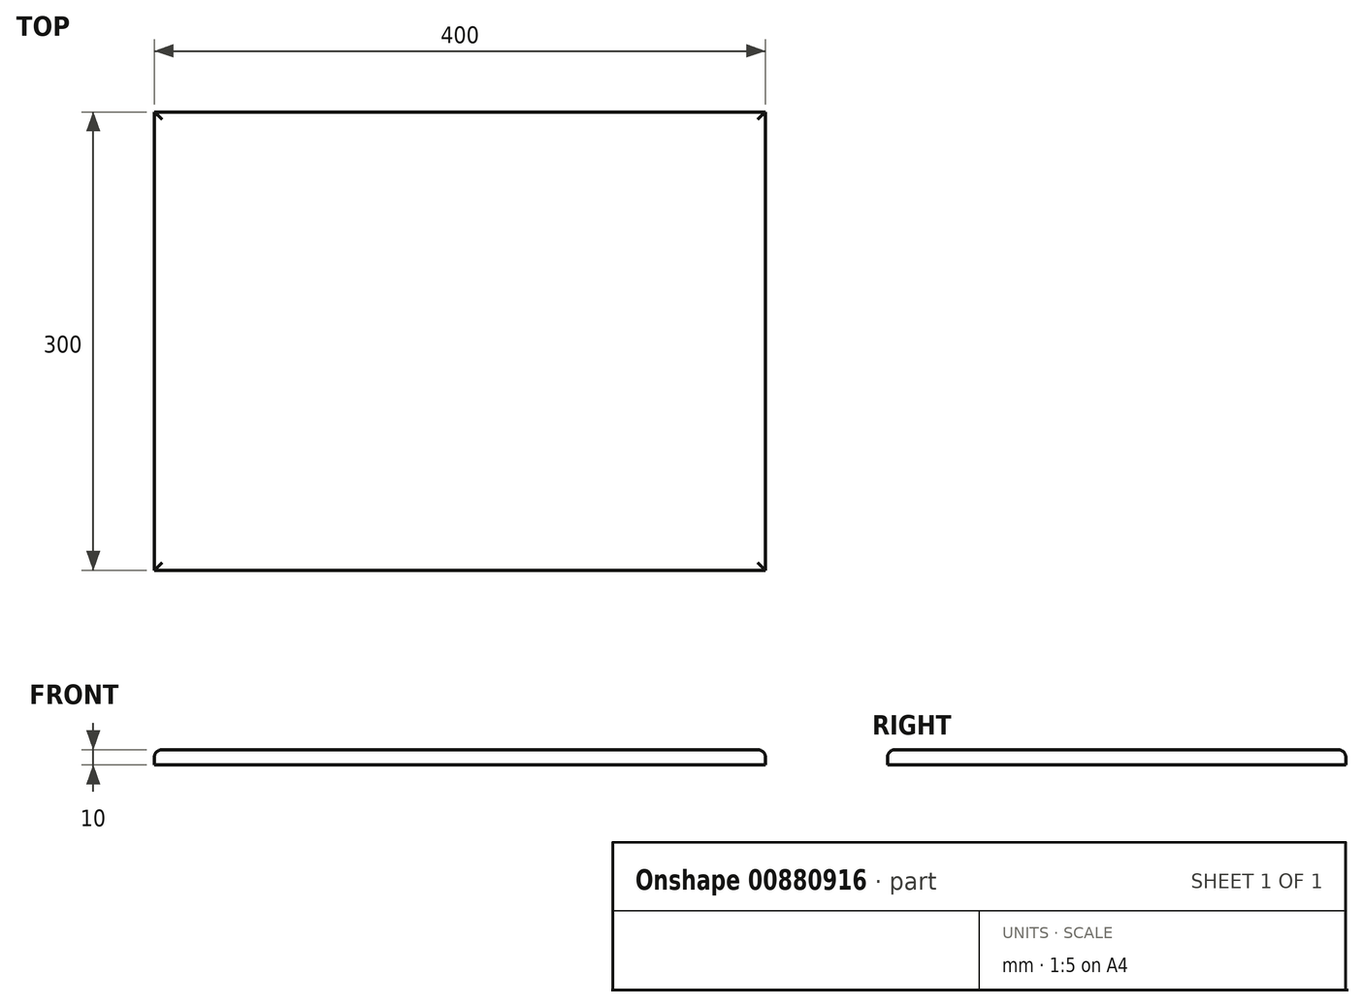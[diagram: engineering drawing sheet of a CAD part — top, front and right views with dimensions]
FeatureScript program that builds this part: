
annotation { "Feature Type Name" : "Feature", "Feature Type Description" : "" }
export const myFeature = defineFeature(function(context is Context, id is Id, definition is map)
    precondition{}
    {
        {
            var Q0;
            Q0=qCreatedBy(makeId("Top.planeOp"),FACE);
            var sketch = newSketch(context, id + "F0", { "sketchPlane" : qUnion([Q0])});
            skLineSegment(sketch, "E0.bottom", {"start": v(-138, 63) * mm, "end": v(138, 63) * mm});
            skLineSegment(sketch, "E0.top", {"start": v(-138, -63) * mm, "end": v(138, -63) * mm});
            skLineSegment(sketch, "E0.left", {"start": v(-138, 63) * mm, "end": v(-138, -63) * mm});
            skLineSegment(sketch, "E0.right", {"start": v(138, 63) * mm, "end": v(138, -63) * mm});
            skPoint(sketch, "E0.middle", {"position": v(0, 0) * mm});
            skSolve(sketch);
        }
        {
            var Q0;
            Q0=makeQuery(id+"F0.imprint","IMPRINT",FACE,{"disambiguationData":[TD([[makeQuery(id+"F0.imprint","IMPRINT",EDGE,{"derivedFrom":sQuery(id+"F0.wireOp",EDGE,"E0.bottom")}),-1.0]])]});
            extrude(context, id + "F1", {"entities" : qUnion([Q0]), "depth" : 12 * mm, "offsetDistance" : 25 * mm});
        }
        {
            var Q0;
            Q0=makeQuery(id+"F1.opExtrude","CAP_EDGE",EDGE,{"disambiguationData":[OSD([sQuery(id+"F0.wireOp",EDGE,"E0.top")])],"isStart":false});
            var Q1;
            Q1=makeQuery(id+"F1.opExtrude","CAP_EDGE",EDGE,{"disambiguationData":[OSD([sQuery(id+"F0.wireOp",EDGE,"E0.left")])],"isStart":false});
            var Q2;
            Q2=makeQuery(id+"F1.opExtrude","CAP_EDGE",EDGE,{"disambiguationData":[OSD([sQuery(id+"F0.wireOp",EDGE,"E0.right")])],"isStart":false});
            var Q3;
            Q3=makeQuery(id+"F1.opExtrude","CAP_EDGE",EDGE,{"disambiguationData":[OSD([sQuery(id+"F0.wireOp",EDGE,"E0.bottom")])],"isStart":false});
            fillet(context, id + "F2", {"entities" : qUnion([Q0, Q1, Q2, Q3]), "radius" : 5 * mm, "tangentPropagation" : true, "allowEdgeOverflow" : false});
        }
        {
            var Q0;
            Q0=makeQuery(id+"F1.opExtrude","SWEPT_BODY",BODY,{"disambiguationData":[OSD([sQuery(id+"F0.wireOp",EDGE,"E0.bottom"),sQuery(id+"F0.wireOp",EDGE,"E0.top"),sQuery(id+"F0.wireOp",EDGE,"E0.left"),sQuery(id+"F0.wireOp",EDGE,"E0.right")])]});
            deleteBodies(context, id + "F3", {"entities" : qUnion([Q0])});
        }
        {
            var Q0;
            Q0=qCreatedBy(makeId("Top.planeOp"),FACE);
            var sketch = newSketch(context, id + "F4", { "sketchPlane" : qUnion([Q0])});
            skLineSegment(sketch, "E1.bottom", {"start": v(-200, 150) * mm, "end": v(200, 150) * mm});
            skLineSegment(sketch, "E1.top", {"start": v(-200, -150) * mm, "end": v(200, -150) * mm});
            skLineSegment(sketch, "E1.left", {"start": v(-200, 150) * mm, "end": v(-200, -150) * mm});
            skLineSegment(sketch, "E1.right", {"start": v(200, 150) * mm, "end": v(200, -150) * mm});
            skPoint(sketch, "E1.middle", {"position": v(0, 0) * mm});
            skSolve(sketch);
        }
        {
            var Q0;
            Q0=makeQuery(id+"F4.imprint","IMPRINT",FACE,{"disambiguationData":[TD([[makeQuery(id+"F4.imprint","IMPRINT",EDGE,{"derivedFrom":sQuery(id+"F4.wireOp",EDGE,"E1.bottom")}),-1.0]])]});
            extrude(context, id + "F5", {"entities" : qUnion([Q0]), "depth" : 10 * mm, "offsetDistance" : 25 * mm});
        }
        {
            var Q0;
            Q0=makeQuery(id+"F5.opExtrude","CAP_EDGE",EDGE,{"disambiguationData":[OSD([sQuery(id+"F4.wireOp",EDGE,"E1.top")])],"isStart":false});
            var Q1;
            Q1=makeQuery(id+"F5.opExtrude","CAP_EDGE",EDGE,{"disambiguationData":[OSD([sQuery(id+"F4.wireOp",EDGE,"E1.left")])],"isStart":false});
            var Q2;
            Q2=makeQuery(id+"F5.opExtrude","CAP_EDGE",EDGE,{"disambiguationData":[OSD([sQuery(id+"F4.wireOp",EDGE,"E1.right")])],"isStart":false});
            var Q3;
            Q3=makeQuery(id+"F5.opExtrude","CAP_EDGE",EDGE,{"disambiguationData":[OSD([sQuery(id+"F4.wireOp",EDGE,"E1.bottom")])],"isStart":false});
            fillet(context, id + "F6", {"entities" : qUnion([Q0, Q1, Q2, Q3]), "radius" : 5 * mm, "tangentPropagation" : true, "allowEdgeOverflow" : false});
        }
    });
